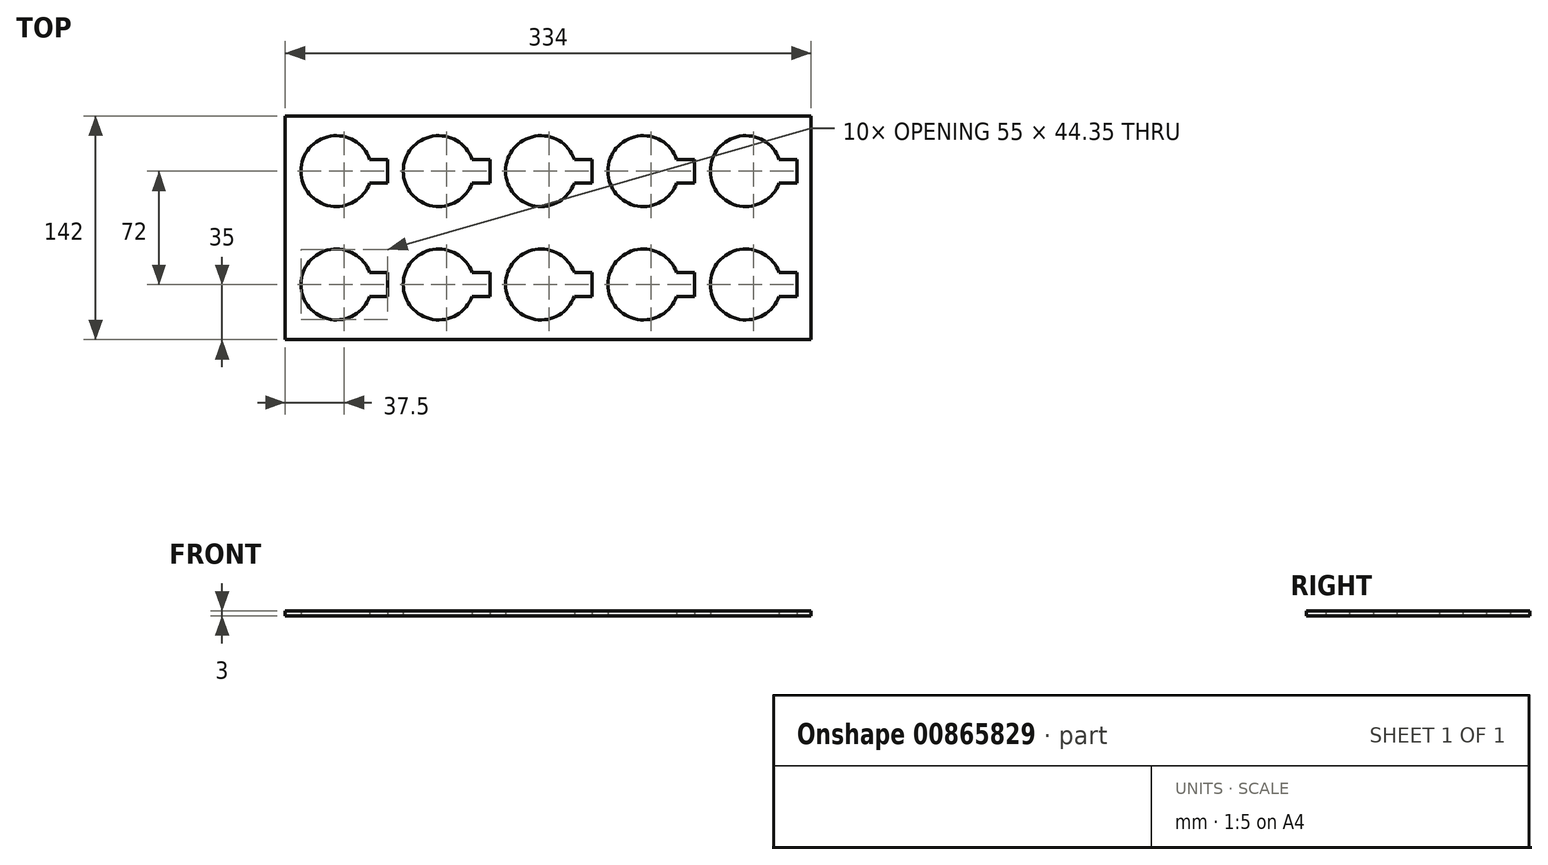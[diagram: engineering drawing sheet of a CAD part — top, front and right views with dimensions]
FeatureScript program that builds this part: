
annotation { "Feature Type Name" : "Feature", "Feature Type Description" : "" }
export const myFeature = defineFeature(function(context is Context, id is Id, definition is map)
    precondition{}
    {
        {
            var Q0;
            Q0=qCreatedBy(makeId("Top.planeOp"),FACE);
            var sketch = newSketch(context, id + "F0", { "sketchPlane" : qUnion([Q0])});
            skLineSegment(sketch, "E0.bottom", {"start": v(-167, 71) * mm, "end": v(167, 71) * mm});
            skLineSegment(sketch, "E0.top", {"start": v(-167, -71) * mm, "end": v(167, -71) * mm});
            skLineSegment(sketch, "E0.left", {"start": v(-167, 71) * mm, "end": v(-167, -71) * mm});
            skLineSegment(sketch, "E0.right", {"start": v(167, 71) * mm, "end": v(167, -71) * mm});
            skArc(sketch, "E1", {"start": v(-113.29, -28.5) * mm, "mid": v(-157, -36) * mm, "end": v(-113.29, -43.5) * mm});
            skLineSegment(sketch, "E2", {"start": v(-113.29, -28.5) * mm, "end": v(-102, -28.5) * mm});
            skLineSegment(sketch, "E3", {"start": v(-102, -28.5) * mm, "end": v(-102, -43.5) * mm});
            skLineSegment(sketch, "E4", {"start": v(-102, -43.5) * mm, "end": v(-113.29, -43.5) * mm});
            skLineSegment(sketch, "E5", {"start": v(-134.5, -36) * mm, "end": v(-167, -36) * mm, "construction": true});
            skPoint(sketch, "E5.endSnap0", {"position": v(-157, -36) * mm});
            skArc(sketch, "E6.0.1.0", {"start": v(-113.29, 43.5) * mm, "mid": v(-157, 36) * mm, "end": v(-113.29, 28.5) * mm});
            skLineSegment(sketch, "E6.0.1.1", {"start": v(-113.29, 43.5) * mm, "end": v(-102, 43.5) * mm});
            skLineSegment(sketch, "E6.0.1.2", {"start": v(-102, 43.5) * mm, "end": v(-102, 28.5) * mm});
            skLineSegment(sketch, "E6.0.1.3", {"start": v(-102, 28.5) * mm, "end": v(-113.29, 28.5) * mm});
            skArc(sketch, "E6.1.0.0", {"start": v(-48.29, -28.5) * mm, "mid": v(-92, -36) * mm, "end": v(-48.29, -43.5) * mm});
            skLineSegment(sketch, "E6.1.0.1", {"start": v(-48.29, -28.5) * mm, "end": v(-37, -28.5) * mm});
            skLineSegment(sketch, "E6.1.0.2", {"start": v(-37, -28.5) * mm, "end": v(-37, -43.5) * mm});
            skLineSegment(sketch, "E6.1.0.3", {"start": v(-37, -43.5) * mm, "end": v(-48.29, -43.5) * mm});
            skArc(sketch, "E6.1.1.0", {"start": v(-48.29, 43.5) * mm, "mid": v(-92, 36) * mm, "end": v(-48.29, 28.5) * mm});
            skLineSegment(sketch, "E6.1.1.1", {"start": v(-48.29, 43.5) * mm, "end": v(-37, 43.5) * mm});
            skLineSegment(sketch, "E6.1.1.2", {"start": v(-37, 43.5) * mm, "end": v(-37, 28.5) * mm});
            skLineSegment(sketch, "E6.1.1.3", {"start": v(-37, 28.5) * mm, "end": v(-48.29, 28.5) * mm});
            skArc(sketch, "E6.2.0.0", {"start": v(16.71, -28.5) * mm, "mid": v(-27, -36) * mm, "end": v(16.71, -43.5) * mm});
            skLineSegment(sketch, "E6.2.0.1", {"start": v(16.71, -28.5) * mm, "end": v(28, -28.5) * mm});
            skLineSegment(sketch, "E6.2.0.2", {"start": v(28, -28.5) * mm, "end": v(28, -43.5) * mm});
            skLineSegment(sketch, "E6.2.0.3", {"start": v(28, -43.5) * mm, "end": v(16.71, -43.5) * mm});
            skArc(sketch, "E6.2.1.0", {"start": v(16.71, 43.5) * mm, "mid": v(-27, 36) * mm, "end": v(16.71, 28.5) * mm});
            skLineSegment(sketch, "E6.2.1.1", {"start": v(16.71, 43.5) * mm, "end": v(28, 43.5) * mm});
            skLineSegment(sketch, "E6.2.1.2", {"start": v(28, 43.5) * mm, "end": v(28, 28.5) * mm});
            skLineSegment(sketch, "E6.2.1.3", {"start": v(28, 28.5) * mm, "end": v(16.71, 28.5) * mm});
            skArc(sketch, "E6.3.0.0", {"start": v(81.71, -28.5) * mm, "mid": v(38, -36) * mm, "end": v(81.71, -43.5) * mm});
            skLineSegment(sketch, "E6.3.0.1", {"start": v(81.71, -28.5) * mm, "end": v(93, -28.5) * mm});
            skLineSegment(sketch, "E6.3.0.2", {"start": v(93, -28.5) * mm, "end": v(93, -43.5) * mm});
            skLineSegment(sketch, "E6.3.0.3", {"start": v(93, -43.5) * mm, "end": v(81.71, -43.5) * mm});
            skArc(sketch, "E6.3.1.0", {"start": v(81.71, 43.5) * mm, "mid": v(38, 36) * mm, "end": v(81.71, 28.5) * mm});
            skLineSegment(sketch, "E6.3.1.1", {"start": v(81.71, 43.5) * mm, "end": v(93, 43.5) * mm});
            skLineSegment(sketch, "E6.3.1.2", {"start": v(93, 43.5) * mm, "end": v(93, 28.5) * mm});
            skLineSegment(sketch, "E6.3.1.3", {"start": v(93, 28.5) * mm, "end": v(81.71, 28.5) * mm});
            skArc(sketch, "E6.4.0.0", {"start": v(146.71, -28.5) * mm, "mid": v(103, -36) * mm, "end": v(146.71, -43.5) * mm});
            skLineSegment(sketch, "E6.4.0.1", {"start": v(146.71, -28.5) * mm, "end": v(158, -28.5) * mm});
            skLineSegment(sketch, "E6.4.0.2", {"start": v(158, -28.5) * mm, "end": v(158, -43.5) * mm});
            skLineSegment(sketch, "E6.4.0.3", {"start": v(158, -43.5) * mm, "end": v(146.71, -43.5) * mm});
            skArc(sketch, "E6.4.1.0", {"start": v(146.71, 43.5) * mm, "mid": v(103, 36) * mm, "end": v(146.71, 28.5) * mm});
            skLineSegment(sketch, "E6.4.1.1", {"start": v(146.71, 43.5) * mm, "end": v(158, 43.5) * mm});
            skLineSegment(sketch, "E6.4.1.2", {"start": v(158, 43.5) * mm, "end": v(158, 28.5) * mm});
            skLineSegment(sketch, "E6.4.1.3", {"start": v(158, 28.5) * mm, "end": v(146.71, 28.5) * mm});
            skLineSegment(sketch, "E6.direction1", {"start": v(-134.5, -36) * mm, "end": v(-69.5, -36) * mm, "construction": true});
            skLineSegment(sketch, "E6.direction2", {"start": v(-134.5, -36) * mm, "end": v(-134.5, 36) * mm, "construction": true});
            skSolve(sketch);
        }
        {
            var Q0;
            Q0 = qSketchRegion(id + "F0", true);
            extrude(context, id + "F1", {"entities" : qUnion([Q0]), "depth" : 3 * mm, "offsetDistance" : 25 * mm});
        }
    });
